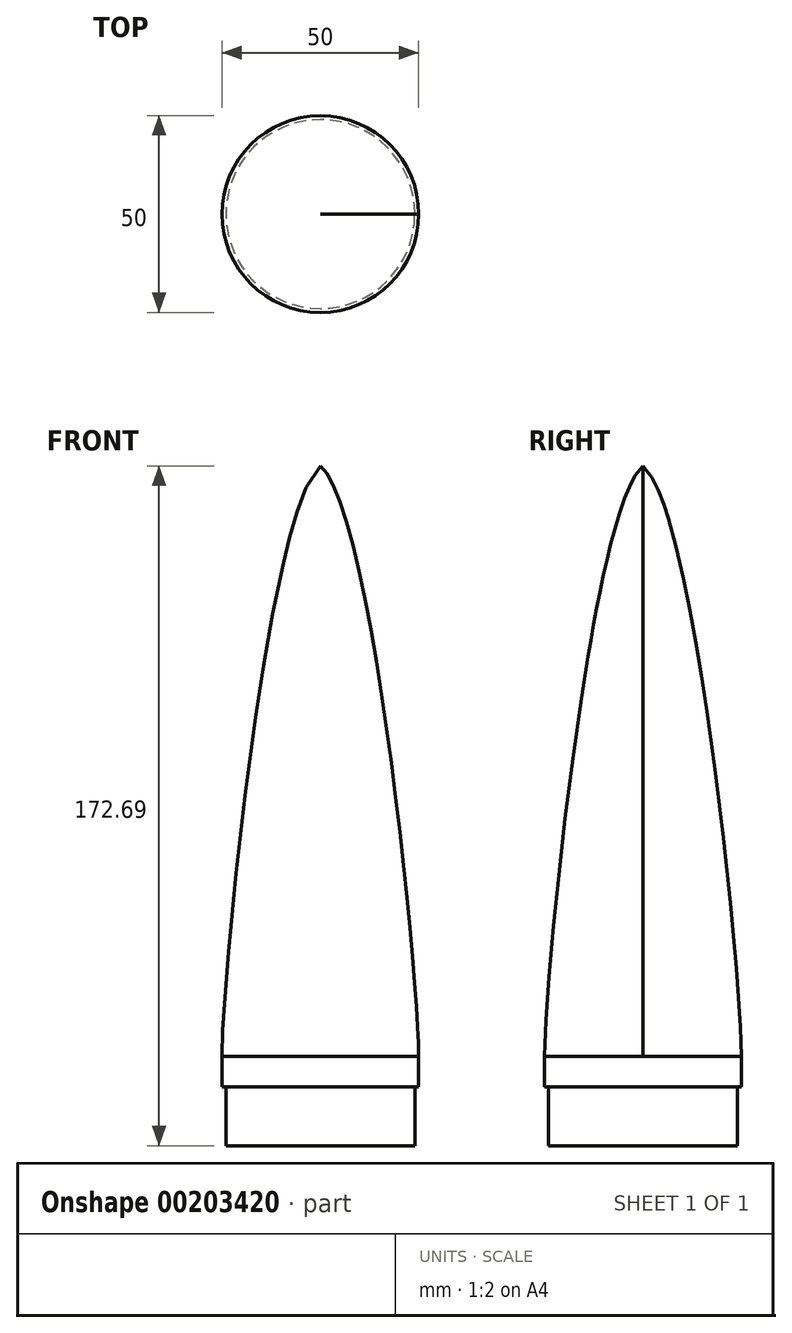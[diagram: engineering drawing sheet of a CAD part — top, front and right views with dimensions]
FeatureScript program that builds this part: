
annotation { "Feature Type Name" : "Feature", "Feature Type Description" : "" }
export const myFeature = defineFeature(function(context is Context, id is Id, definition is map)
    precondition{}
    {
        {
            var Q0;
            Q0=qCreatedBy(makeId("Front.planeOp"),FACE);
            var sketch = newSketch(context, id + "F0", { "sketchPlane" : qUnion([Q0])});
            skLineSegment(sketch, "E0", {"start": v(0, -22.69) * mm, "end": v(24, -22.69) * mm});
            skLineSegment(sketch, "E1", {"start": v(24, -7.69) * mm, "end": v(24, -22.69) * mm});
            skLineSegment(sketch, "E2", {"start": v(24, -7.69) * mm, "end": v(25, -7.69) * mm});
            skLineSegment(sketch, "E3", {"start": v(25, -7.69) * mm, "end": v(25, -7.69) * mm});
            skLineSegment(sketch, "E4", {"start": v(25, -7.69) * mm, "end": v(25, 0) * mm});
            skLineSegment(sketch, "E5", {"start": v(25, 0) * mm, "end": v(25, 0) * mm});
            skLineSegment(sketch, "E6", {"start": v(25, 0) * mm, "end": v(0, 150) * mm, "construction": true});
            skLineSegment(sketch, "E7", {"start": v(0, 150) * mm, "end": v(0, -22.69) * mm});
            skFitSpline(sketch, "E8", {"points": [v(25, 0) * mm, v(0, 150) * mm], "startDerivative": vector(0, 62.43) * mm, "endDerivative": vector(-39.48, 31.47) * mm});
            skLineSegment(sketch, "E9", {"start": v(25, 0) * mm, "end": v(25, 41.95) * mm, "construction": true});
            skLineSegment(sketch, "E10", {"start": v(0, -22.69) * mm, "end": v(0, 210.1) * mm, "construction": true});
            skSolve(sketch);
        }
        {
            var Q0;
            Q0=makeQuery(id+"F0.imprint","IMPRINT",FACE,{"disambiguationData":[TD([[makeQuery(id+"F0.imprint","IMPRINT",EDGE,{"derivedFrom":sQuery(id+"F0.wireOp",EDGE,"E0")}),1.0]])]});
            var Q1;
            Q1=sQuery(id+"F0.wireOp",EDGE,"E10");
            revolve(context, id + "F1", {"entities" : qUnion([Q0]), "axis" : qUnion([Q1]), "revolveType" : RevolveType.FULL});
        }
    });
